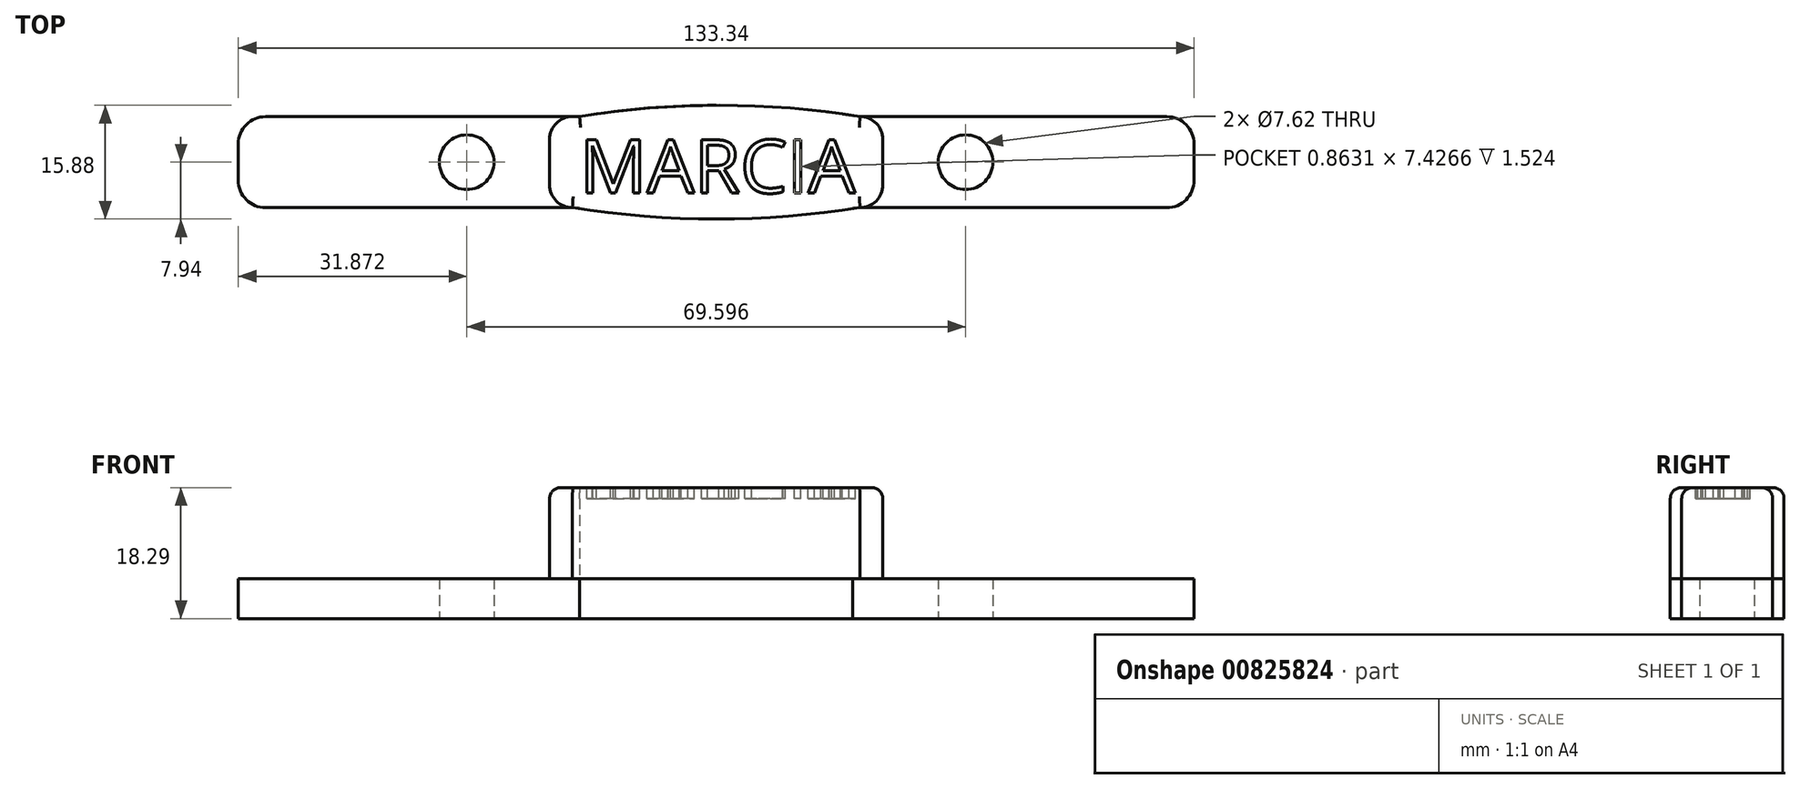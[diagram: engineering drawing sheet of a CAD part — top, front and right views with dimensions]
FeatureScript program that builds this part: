
annotation { "Feature Type Name" : "Feature", "Feature Type Description" : "" }
export const myFeature = defineFeature(function(context is Context, id is Id, definition is map)
    precondition{}
    {
        {
            var Q0;
            Q0=qCreatedBy(makeId("Top.planeOp"),FACE);
            var sketch = newSketch(context, id + "F0", { "sketchPlane" : qUnion([Q0])});
            skLineSegment(sketch, "E0.bottom", {"start": v(62.87, -6.35) * mm, "end": v(19.05, -6.35) * mm});
            skLineSegment(sketch, "E0.top", {"start": v(62.87, 6.35) * mm, "end": v(19.05, 6.35) * mm});
            skLineSegment(sketch, "E0.left", {"start": v(66.68, -2.54) * mm, "end": v(66.68, 2.54) * mm});
            skLineSegment(sketch, "E0.right", {"start": v(-66.68, -2.54) * mm, "end": v(-66.68, 2.54) * mm});
            skPoint(sketch, "E0.middle", {"position": v(0, 0) * mm});
            skPoint(sketch, "E1", {"position": v(0, 7.94) * mm});
            skPoint(sketch, "E2", {"position": v(0, -7.94) * mm});
            skPoint(sketch, "E3", {"position": v(-19.05, 6.35) * mm});
            skPoint(sketch, "E4", {"position": v(-19.05, -6.35) * mm});
            skPoint(sketch, "E5", {"position": v(19.05, 6.35) * mm});
            skPoint(sketch, "E6", {"position": v(19.05, -6.35) * mm});
            skArc(sketch, "E7", {"start": v(19.05, 6.35) * mm, "mid": v(0, 7.94) * mm, "end": v(-19.05, 6.35) * mm});
            skArc(sketch, "E8", {"start": v(-19.05, -6.35) * mm, "mid": v(0, -7.94) * mm, "end": v(19.05, -6.35) * mm});
            skLineSegment(sketch, "E9.trimOffspring", {"start": v(-19.05, 6.35) * mm, "end": v(-62.87, 6.35) * mm});
            skLineSegment(sketch, "E10.trimOffspring", {"start": v(-19.05, -6.35) * mm, "end": v(-62.87, -6.35) * mm});
            skPoint(sketch, "E11.visualSharp", {"position": v(-66.68, 6.35) * mm});
            skArc(sketch, "E11.filletArc", {"start": v(-62.87, 6.35) * mm, "mid": v(-65.56, 5.23) * mm, "end": v(-66.68, 2.54) * mm});
            skPoint(sketch, "E12.visualSharp", {"position": v(-66.68, -6.35) * mm});
            skArc(sketch, "E12.filletArc", {"start": v(-66.68, -2.54) * mm, "mid": v(-65.56, -5.23) * mm, "end": v(-62.87, -6.35) * mm});
            skPoint(sketch, "E13.visualSharp", {"position": v(66.68, 6.35) * mm});
            skArc(sketch, "E13.filletArc", {"start": v(66.68, 2.54) * mm, "mid": v(65.56, 5.23) * mm, "end": v(62.87, 6.35) * mm});
            skPoint(sketch, "E14.visualSharp", {"position": v(66.68, -6.35) * mm});
            skArc(sketch, "E14.filletArc", {"start": v(62.87, -6.35) * mm, "mid": v(65.56, -5.23) * mm, "end": v(66.68, -2.54) * mm});
            skCircle(sketch, "E15", {"center": v(-34.8, 0) * mm, "radius": 3.81 * mm});
            skCircle(sketch, "E16.MirrorC", {"center": v(34.8, 0) * mm, "radius": 3.81 * mm});
            skSolve(sketch);
        }
        {
            var Q0;
            Q0 = qSketchRegion(id + "F0", true);
            extrude(context, id + "F1", {"entities" : qUnion([Q0]), "depth" : 5.6 * mm, "offsetDistance" : 25.4 * mm});
        }
        {
            var Q0;
            Q0=makeQuery(id+"F1.opExtrude","CAP_FACE",FACE,{"disambiguationData":[OSD([sQuery(id+"F0.wireOp",EDGE,"E0.bottom"),sQuery(id+"F0.wireOp",EDGE,"E0.top"),sQuery(id+"F0.wireOp",EDGE,"E0.left"),sQuery(id+"F0.wireOp",EDGE,"E0.right"),sQuery(id+"F0.wireOp",EDGE,"E7"),sQuery(id+"F0.wireOp",EDGE,"E8"),sQuery(id+"F0.wireOp",EDGE,"E9.trimOffspring"),sQuery(id+"F0.wireOp",EDGE,"E10.trimOffspring"),sQuery(id+"F0.wireOp",EDGE,"E11.filletArc"),sQuery(id+"F0.wireOp",EDGE,"E12.filletArc"),sQuery(id+"F0.wireOp",EDGE,"E13.filletArc"),sQuery(id+"F0.wireOp",EDGE,"E14.filletArc"),sQuery(id+"F0.wireOp",EDGE,"E15"),sQuery(id+"F0.wireOp",EDGE,"E16.MirrorC")])],"isStart":false});
            var sketch = newSketch(context, id + "F2", { "sketchPlane" : qUnion([Q0])});
            skLineSegment(sketch, "E17.top", {"start": v(-20.07, 6.35) * mm, "end": v(-19.05, 6.35) * mm});
            skLineSegment(sketch, "E17.left", {"start": v(-23.24, -3.18) * mm, "end": v(-23.24, 3.18) * mm});
            skLineSegment(sketch, "E17.right", {"start": v(23.24, -3.18) * mm, "end": v(23.24, 3.18) * mm});
            skPoint(sketch, "E17.middle", {"position": v(0, 0) * mm});
            skPoint(sketch, "E18.visualSharp", {"position": v(-23.24, 6.35) * mm});
            skArc(sketch, "E18.filletArc", {"start": v(-20.07, 6.35) * mm, "mid": v(-22.31, 5.42) * mm, "end": v(-23.24, 3.18) * mm});
            skPoint(sketch, "E19.visualSharp", {"position": v(-23.24, -6.35) * mm});
            skArc(sketch, "E19.filletArc", {"start": v(-23.24, -3.18) * mm, "mid": v(-22.31, -5.42) * mm, "end": v(-20.07, -6.35) * mm});
            skPoint(sketch, "E20.visualSharp", {"position": v(23.24, 6.35) * mm});
            skArc(sketch, "E20.filletArc", {"start": v(23.24, 3.18) * mm, "mid": v(22.31, 5.42) * mm, "end": v(20.07, 6.35) * mm});
            skPoint(sketch, "E21.visualSharp", {"position": v(23.24, -6.35) * mm});
            skArc(sketch, "E21.filletArc", {"start": v(20.07, -6.35) * mm, "mid": v(22.31, -5.42) * mm, "end": v(23.24, -3.18) * mm});
            skArc(sketch, "E22", {"start": v(20.07, 6.35) * mm, "mid": v(0.5, 7.94) * mm, "end": v(-19.05, 6.35) * mm});
            skArc(sketch, "E23", {"start": v(-20.07, -6.35) * mm, "mid": v(0, -7.94) * mm, "end": v(20.07, -6.35) * mm});
            skSolve(sketch);
        }
        {
            var Q0;
            Q0 = qSketchRegion(id + "F2", true);
            extrude(context, id + "F3", {"entities" : qUnion([Q0]), "operationType" : NewBodyOperationType.ADD, "depth" : 12.7 * mm, "offsetDistance" : 25.4 * mm});
        }
        {
            var Q0;
            Q0=makeQuery(id+"F3.opExtrude","CAP_FACE",FACE,{"disambiguationData":[OSD([sQuery(id+"F2.wireOp",EDGE,"E17.top"),sQuery(id+"F2.wireOp",EDGE,"E17.left"),sQuery(id+"F2.wireOp",EDGE,"E17.right"),sQuery(id+"F2.wireOp",EDGE,"E18.filletArc"),sQuery(id+"F2.wireOp",EDGE,"E19.filletArc"),sQuery(id+"F2.wireOp",EDGE,"E20.filletArc"),sQuery(id+"F2.wireOp",EDGE,"E21.filletArc"),sQuery(id+"F2.wireOp",EDGE,"E22"),sQuery(id+"F2.wireOp",EDGE,"E23")])],"isStart":false});
            var sketch = newSketch(context, id + "F4", { "sketchPlane" : qUnion([Q0])});
            skText(sketch, "E24", { "text": "MARCIA", "fontName": "OpenSans-Regular.ttf"});
            const initialGuessF4  = {"E24": [-0.01905, -0.00431, 1, 0, 0.00749]};
            skSetInitialGuess(sketch, initialGuessF4);
            skSolve(sketch);
        }
        {
            var Q0;
            Q0 = qSketchRegion(id + "F4", true);
            extrude(context, id + "F5", {"entities" : qUnion([Q0]), "operationType" : NewBodyOperationType.REMOVE, "oppositeDirection" : true, "depth" : 1.52 * mm, "offsetDistance" : 25.4 * mm});
        }
        {
            var Q0;
            Q0=makeQuery(id+"F3.opExtrude","CAP_EDGE",EDGE,{"disambiguationData":[OSD([sQuery(id+"F2.wireOp",EDGE,"E23")])],"isStart":false});
            var Q1;
            Q1=makeQuery(id+"F3.opExtrude","CAP_EDGE",EDGE,{"disambiguationData":[OSD([sQuery(id+"F2.wireOp",EDGE,"E21.filletArc")])],"isStart":false});
            var Q2;
            Q2=makeQuery(id+"F3.opExtrude","CAP_EDGE",EDGE,{"disambiguationData":[OSD([sQuery(id+"F2.wireOp",EDGE,"E17.right")])],"isStart":false});
            var Q3;
            Q3=makeQuery(id+"F3.opExtrude","CAP_EDGE",EDGE,{"disambiguationData":[OSD([sQuery(id+"F2.wireOp",EDGE,"E18.filletArc")])],"isStart":false});
            var Q4;
            Q4=makeQuery(id+"F3.opExtrude","CAP_EDGE",EDGE,{"disambiguationData":[OSD([sQuery(id+"F2.wireOp",EDGE,"E17.left")])],"isStart":false});
            var Q5;
            Q5=makeQuery(id+"F3.opExtrude","CAP_EDGE",EDGE,{"disambiguationData":[OSD([sQuery(id+"F2.wireOp",EDGE,"E19.filletArc")])],"isStart":false});
            var Q6;
            Q6=makeQuery(id+"F3.opExtrude","CAP_EDGE",EDGE,{"disambiguationData":[OSD([sQuery(id+"F2.wireOp",EDGE,"E22")])],"isStart":false});
            fillet(context, id + "F6", {"entities" : qUnion([Q0, Q1, Q2, Q3, Q4, Q5, Q6]), "radius" : 1.52 * mm, "tangentPropagation" : true, "allowEdgeOverflow" : false});
        }
    });
